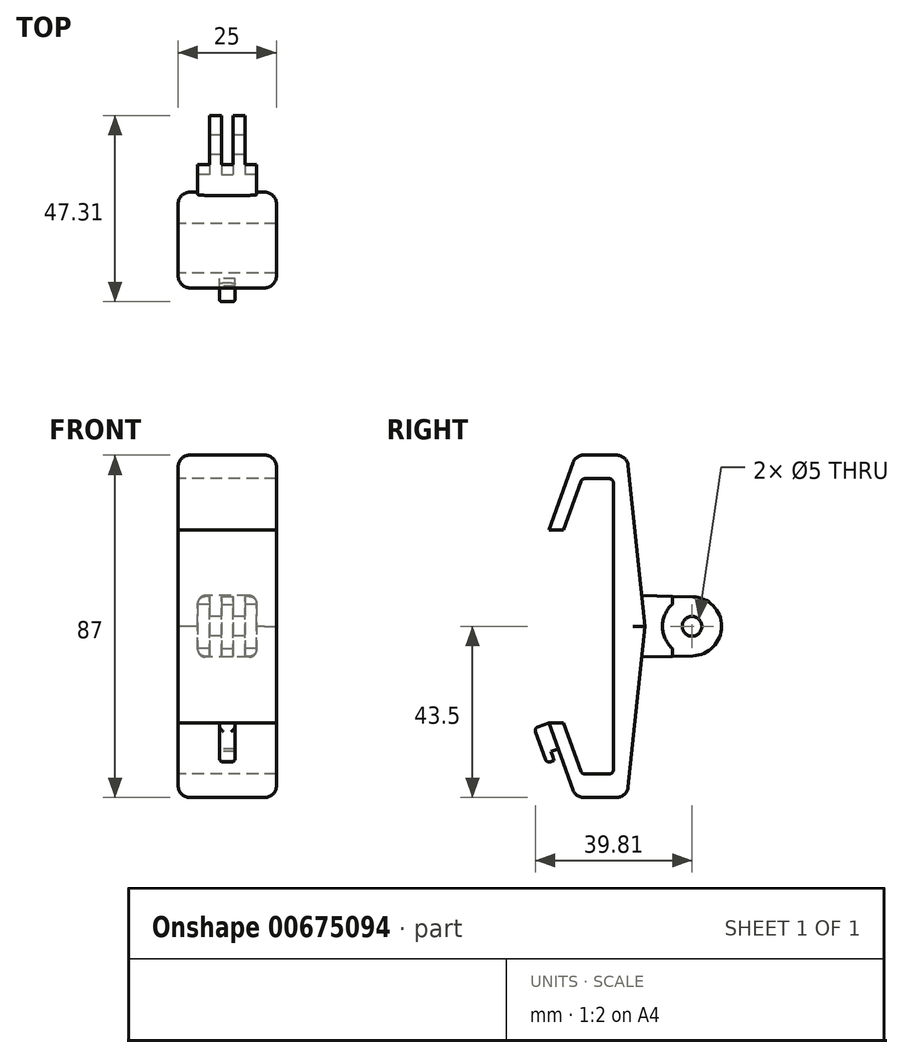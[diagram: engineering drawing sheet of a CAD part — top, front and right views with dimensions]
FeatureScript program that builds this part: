
annotation { "Feature Type Name" : "Feature", "Feature Type Description" : "" }
export const myFeature = defineFeature(function(context is Context, id is Id, definition is map)
    precondition{}
    {
        {
            var Q0;
            Q0=qCreatedBy(makeId("Right.planeOp"),FACE);
            var sketch = newSketch(context, id + "F0", { "sketchPlane" : qUnion([Q0])});
            skLineSegment(sketch, "E0", {"start": v(0, 37.5) * mm, "end": v(0, -37.5) * mm});
            skLineSegment(sketch, "E1", {"start": v(0, -37.5) * mm, "end": v(-8, -37.5) * mm});
            skLineSegment(sketch, "E2", {"start": v(-8, -37.5) * mm, "end": v(-12.6, -24.5) * mm});
            skLineSegment(sketch, "E3", {"start": v(-12.6, -24.5) * mm, "end": v(-16.31, -24.5) * mm});
            skLineSegment(sketch, "E4", {"start": v(-16.31, -24.5) * mm, "end": v(-9.59, -43.5) * mm});
            skLineSegment(sketch, "E5", {"start": v(-9.59, -43.5) * mm, "end": v(3.5, -43.5) * mm});
            skLineSegment(sketch, "E6", {"start": v(3.5, -43.5) * mm, "end": v(8, 0) * mm});
            skLineSegment(sketch, "E7", {"start": v(8, 0) * mm, "end": v(3.5, 43.5) * mm});
            skLineSegment(sketch, "E8", {"start": v(3.5, 43.5) * mm, "end": v(-9.59, 43.5) * mm});
            skLineSegment(sketch, "E9", {"start": v(-9.59, 43.5) * mm, "end": v(-16.31, 24.5) * mm});
            skLineSegment(sketch, "E10", {"start": v(-16.31, 24.5) * mm, "end": v(-12.6, 24.5) * mm});
            skLineSegment(sketch, "E11", {"start": v(-12.6, 24.5) * mm, "end": v(-8, 37.5) * mm});
            skLineSegment(sketch, "E12", {"start": v(-8, 37.5) * mm, "end": v(0, 37.5) * mm});
            skSolve(sketch);
        }
        {
            var Q0;
            Q0=makeQuery(id+"F0.imprint","IMPRINT",FACE,{"disambiguationData":[TD([[makeQuery(id+"F0.imprint","IMPRINT",EDGE,{"derivedFrom":sQuery(id+"F0.wireOp",EDGE,"E0")}),1.0]])]});
            extrude(context, id + "F1", {"entities" : qUnion([Q0]), "endBound" : BoundingType.SYMMETRIC, "depth" : 25 * mm, "offsetDistance" : 25 * mm});
        }
        {
            var Q0;
            Q0=qCreatedBy(makeId("Right.planeOp"),FACE);
            var sketch = newSketch(context, id + "F2", { "sketchPlane" : qUnion([Q0])});
            skCircle(sketch, "E13", {"center": v(20, 0) * mm, "radius": 2.5 * mm});
            skCircle(sketch, "E14", {"center": v(20, 0) * mm, "radius": 7.5 * mm});
            skLineSegment(sketch, "E15.0", {"start": v(8, 0) * mm, "end": v(3.5, 43.5) * mm});
            skLineSegment(sketch, "E16.0", {"start": v(3.5, -43.5) * mm, "end": v(8, 0) * mm});
            skLineSegment(sketch, "E17", {"start": v(7.19, 7.84) * mm, "end": v(20.2, 7.5) * mm});
            skLineSegment(sketch, "E18", {"start": v(7.19, -7.84) * mm, "end": v(20.2, -7.5) * mm});
            skLineSegment(sketch, "E19", {"start": v(15, 7.63) * mm, "end": v(15, -7.63) * mm});
            skSolve(sketch);
        }
        {
            var Q0;
            {var subQ7=sQuery(id+"F2.wireOp",EDGE,"E19");var subQ9=sQuery(id+"F2.wireOp",EDGE,"E14");var subQ10=makeQuery(id+"F2.imprint","INTERSECT",VERTEX,{"disambiguationData":[OD(0.0)],"derivedFrom":[subQ9,subQ7]});Q0=makeQuery(id+"F2.imprint","IMPRINT",FACE,{"disambiguationData":[TD([[makeQuery(id+"F2.imprint","IMPRINT",EDGE,{"disambiguationData":[TD([[subQ10,-1.0]])],"derivedFrom":subQ9}),-1.0]])]});}
            extrude(context, id + "F3", {"entities" : qUnion([Q0]), "operationType" : NewBodyOperationType.ADD, "endBound" : BoundingType.SYMMETRIC, "depth" : 15 * mm, "offsetDistance" : 25 * mm});
        }
        {
            var Q0;
            {var subQ0=sQuery(id+"F2.wireOp",EDGE,"E17");var subQ1=sQuery(id+"F2.wireOp",EDGE,"E14");var subQ2=makeQuery(id+"F2.imprint","INTERSECT",VERTEX,{"derivedFrom":[subQ1,subQ0]});Q0=makeQuery(id+"F2.imprint","IMPRINT",FACE,{"disambiguationData":[TD([[makeQuery(id+"F2.imprint","IMPRINT",EDGE,{"disambiguationData":[TD([[subQ2,-1.0]])],"derivedFrom":subQ1}),-1.0]])]});}
            var Q1;
            Q1=makeQuery(id+"F2.imprint","IMPRINT",FACE,{"disambiguationData":[TD([[makeQuery(id+"F2.imprint","IMPRINT",EDGE,{"derivedFrom":sQuery(id+"F2.wireOp",EDGE,"E13")}),-1.0]])]});
            var Q2;
            {var subQ0=sQuery(id+"F2.wireOp",EDGE,"E19");var subQ1=sQuery(id+"F2.wireOp",EDGE,"E14");var subQ2=makeQuery(id+"F2.imprint","INTERSECT",VERTEX,{"disambiguationData":[OD(0.0)],"derivedFrom":[subQ1,subQ0]});Q2=makeQuery(id+"F2.imprint","IMPRINT",FACE,{"disambiguationData":[TD([[makeQuery(id+"F2.imprint","IMPRINT",EDGE,{"disambiguationData":[TD([[subQ2,-1.0]])],"derivedFrom":subQ1}),1.0]])]});}
            var Q3;
            {var subQ0=sQuery(id+"F2.wireOp",EDGE,"E18");var subQ1=sQuery(id+"F2.wireOp",EDGE,"E14");var subQ2=makeQuery(id+"F2.imprint","INTERSECT",VERTEX,{"derivedFrom":[subQ1,subQ0]});Q3=makeQuery(id+"F2.imprint","IMPRINT",FACE,{"disambiguationData":[TD([[makeQuery(id+"F2.imprint","IMPRINT",EDGE,{"disambiguationData":[TD([[subQ2,1.0]])],"derivedFrom":subQ1}),-1.0]])]});}
            extrude(context, id + "F4", {"entities" : qUnion([Q0, Q1, Q2, Q3]), "operationType" : NewBodyOperationType.ADD, "endBound" : BoundingType.SYMMETRIC, "depth" : 9 * mm, "offsetDistance" : 25 * mm});
        }
        {
            var Q0;
            {var subQ0=sQuery(id+"F2.wireOp",EDGE,"E17");var subQ1=sQuery(id+"F2.wireOp",EDGE,"E14");var subQ2=makeQuery(id+"F2.imprint","INTERSECT",VERTEX,{"derivedFrom":[subQ1,subQ0]});Q0=makeQuery(id+"F2.imprint","IMPRINT",FACE,{"disambiguationData":[TD([[makeQuery(id+"F2.imprint","IMPRINT",EDGE,{"disambiguationData":[TD([[subQ2,-1.0]])],"derivedFrom":subQ1}),-1.0]])]});}
            var Q1;
            {var subQ0=sQuery(id+"F2.wireOp",EDGE,"E18");var subQ1=sQuery(id+"F2.wireOp",EDGE,"E14");var subQ2=makeQuery(id+"F2.imprint","INTERSECT",VERTEX,{"derivedFrom":[subQ1,subQ0]});Q1=makeQuery(id+"F2.imprint","IMPRINT",FACE,{"disambiguationData":[TD([[makeQuery(id+"F2.imprint","IMPRINT",EDGE,{"disambiguationData":[TD([[subQ2,1.0]])],"derivedFrom":subQ1}),-1.0]])]});}
            var Q2;
            Q2=makeQuery(id+"F2.imprint","IMPRINT",FACE,{"disambiguationData":[TD([[makeQuery(id+"F2.imprint","IMPRINT",EDGE,{"derivedFrom":sQuery(id+"F2.wireOp",EDGE,"E13")}),-1.0]])]});
            var Q3;
            {var subQ0=sQuery(id+"F2.wireOp",EDGE,"E19");var subQ1=sQuery(id+"F2.wireOp",EDGE,"E14");var subQ2=makeQuery(id+"F2.imprint","INTERSECT",VERTEX,{"disambiguationData":[OD(0.0)],"derivedFrom":[subQ1,subQ0]});Q3=makeQuery(id+"F2.imprint","IMPRINT",FACE,{"disambiguationData":[TD([[makeQuery(id+"F2.imprint","IMPRINT",EDGE,{"disambiguationData":[TD([[subQ2,-1.0]])],"derivedFrom":subQ1}),1.0]])]});}
            extrude(context, id + "F5", {"entities" : qUnion([Q0, Q1, Q2, Q3]), "operationType" : NewBodyOperationType.REMOVE, "endBound" : BoundingType.SYMMETRIC, "oppositeDirection" : true, "depth" : 3 * mm, "offsetDistance" : 25 * mm});
        }
        {
            var Q0;
            Q0=makeQuery(id+"F1.opExtrude","CAP_EDGE",EDGE,{"disambiguationData":[OSD([sQuery(id+"F0.wireOp",EDGE,"E7")])],"isStart":false});
            var Q1;
            Q1=makeQuery(id+"F1.opExtrude","CAP_EDGE",EDGE,{"disambiguationData":[OSD([sQuery(id+"F0.wireOp",EDGE,"E6")])],"isStart":false});
            var Q2;
            Q2=makeQuery(id+"F1.opExtrude","CAP_EDGE",EDGE,{"disambiguationData":[OSD([sQuery(id+"F0.wireOp",EDGE,"E5")])],"isStart":false});
            var Q3;
            Q3=makeQuery(id+"F1.opExtrude","CAP_EDGE",EDGE,{"disambiguationData":[OSD([sQuery(id+"F0.wireOp",EDGE,"E4")])],"isStart":false});
            var Q4;
            Q4=makeQuery(id+"F1.opExtrude","SWEPT_EDGE",EDGE,{"disambiguationData":[OSD([sQuery(id+"F0.wireOp",EDGE,"E4"),sQuery(id+"F0.wireOp",EDGE,"E5")])]});
            var Q5;
            Q5=makeQuery(id+"F1.opExtrude","CAP_EDGE",EDGE,{"disambiguationData":[OSD([sQuery(id+"F0.wireOp",EDGE,"E4")])],"isStart":true});
            var Q6;
            Q6=makeQuery(id+"F1.opExtrude","CAP_EDGE",EDGE,{"disambiguationData":[OSD([sQuery(id+"F0.wireOp",EDGE,"E6")])],"isStart":true});
            var Q7;
            Q7=makeQuery(id+"F1.opExtrude","CAP_EDGE",EDGE,{"disambiguationData":[OSD([sQuery(id+"F0.wireOp",EDGE,"E5")])],"isStart":true});
            var Q8;
            Q8=makeQuery(id+"F1.opExtrude","CAP_EDGE",EDGE,{"disambiguationData":[OSD([sQuery(id+"F0.wireOp",EDGE,"E7")])],"isStart":true});
            var Q9;
            Q9=makeQuery(id+"F1.opExtrude","SWEPT_EDGE",EDGE,{"disambiguationData":[OSD([sQuery(id+"F0.wireOp",EDGE,"E7"),sQuery(id+"F0.wireOp",EDGE,"E8")])]});
            var Q10;
            Q10=makeQuery(id+"F1.opExtrude","SWEPT_EDGE",EDGE,{"disambiguationData":[OSD([sQuery(id+"F0.wireOp",EDGE,"E5"),sQuery(id+"F0.wireOp",EDGE,"E6")])]});
            var Q11;
            Q11=makeQuery(id+"F1.opExtrude","SWEPT_EDGE",EDGE,{"disambiguationData":[OSD([sQuery(id+"F0.wireOp",EDGE,"E8"),sQuery(id+"F0.wireOp",EDGE,"E9")])]});
            var Q12;
            Q12=makeQuery(id+"F1.opExtrude","CAP_EDGE",EDGE,{"disambiguationData":[OSD([sQuery(id+"F0.wireOp",EDGE,"E8")])],"isStart":true});
            var Q13;
            Q13=makeQuery(id+"F1.opExtrude","CAP_EDGE",EDGE,{"disambiguationData":[OSD([sQuery(id+"F0.wireOp",EDGE,"E9")])],"isStart":true});
            var Q14;
            Q14=makeQuery(id+"F1.opExtrude","CAP_EDGE",EDGE,{"disambiguationData":[OSD([sQuery(id+"F0.wireOp",EDGE,"E9")])],"isStart":false});
            var Q15;
            Q15=makeQuery(id+"F1.opExtrude","CAP_EDGE",EDGE,{"disambiguationData":[OSD([sQuery(id+"F0.wireOp",EDGE,"E8")])],"isStart":false});
            fillet(context, id + "F6", {"entities" : qUnion([Q0, Q1, Q2, Q3, Q4, Q5, Q6, Q7, Q8, Q9, Q10, Q11, Q12, Q13, Q14, Q15]), "radius" : 3 * mm, "tangentPropagation" : true, "allowEdgeOverflow" : false});
        }
        {
            var Q0;
            Q0=makeQuery(id+"F3.opExtrude","SWEPT_EDGE",EDGE,{"disambiguationData":[OSD([sQuery(id+"F2.wireOp",EDGE,"E15.0"),sQuery(id+"F2.wireOp",EDGE,"E17")])]});
            var Q1;
            Q1=makeQuery(id+"F3.opExtrude","CAP_EDGE",EDGE,{"disambiguationData":[OSD([sQuery(id+"F2.wireOp",EDGE,"E15.0")])],"isStart":true});
            var Q2;
            Q2=makeQuery(id+"F3.opExtrude","CAP_EDGE",EDGE,{"disambiguationData":[OSD([sQuery(id+"F2.wireOp",EDGE,"E16.0")])],"isStart":true});
            var Q3;
            Q3=makeQuery(id+"F3.opExtrude","SWEPT_EDGE",EDGE,{"disambiguationData":[OSD([sQuery(id+"F2.wireOp",EDGE,"E16.0"),sQuery(id+"F2.wireOp",EDGE,"E18")])]});
            var Q4;
            Q4=makeQuery(id+"F3.opExtrude","CAP_EDGE",EDGE,{"disambiguationData":[OSD([sQuery(id+"F2.wireOp",EDGE,"E16.0")])],"isStart":false});
            var Q5;
            Q5=makeQuery(id+"F3.opExtrude","CAP_EDGE",EDGE,{"disambiguationData":[OSD([sQuery(id+"F2.wireOp",EDGE,"E15.0")])],"isStart":false});
            var Q6;
            Q6=makeQuery(id+"F3.opExtrude","CAP_EDGE",EDGE,{"disambiguationData":[OSD([sQuery(id+"F2.wireOp",EDGE,"E17")])],"isStart":false});
            var Q7;
            Q7=makeQuery(id+"F3.opExtrude","CAP_EDGE",EDGE,{"disambiguationData":[OSD([sQuery(id+"F2.wireOp",EDGE,"E18")])],"isStart":false});
            var Q8;
            Q8=makeQuery(id+"F3.opExtrude","CAP_EDGE",EDGE,{"disambiguationData":[OSD([sQuery(id+"F2.wireOp",EDGE,"E18")])],"isStart":true});
            var Q9;
            Q9=makeQuery(id+"F3.opExtrude","CAP_EDGE",EDGE,{"disambiguationData":[OSD([sQuery(id+"F2.wireOp",EDGE,"E17")])],"isStart":true});
            fillet(context, id + "F7", {"entities" : qUnion([Q0, Q1, Q2, Q3, Q4, Q5, Q6, Q7, Q8, Q9]), "radius" : 2 * mm, "tangentPropagation" : true, "allowEdgeOverflow" : false});
        }
        {
            var Q0;
            Q0=makeQuery(id+"F1.opExtrude","SWEPT_FACE",FACE,{"disambiguationData":[OSD([sQuery(id+"F0.wireOp",EDGE,"E4")])]});
            var sketch = newSketch(context, id + "F8", { "sketchPlane" : qUnion([Q0])});
            skLineSegment(sketch, "E20.bottom", {"start": v(-2, -17.66) * mm, "end": v(2, -17.66) * mm});
            skLineSegment(sketch, "E20.top", {"start": v(-2, -27.16) * mm, "end": v(2, -27.16) * mm});
            skLineSegment(sketch, "E20.left", {"start": v(-2, -17.66) * mm, "end": v(-2, -27.16) * mm});
            skLineSegment(sketch, "E20.right", {"start": v(2, -17.66) * mm, "end": v(2, -27.16) * mm});
            skPoint(sketch, "E20.middle", {"position": v(0, -22.4) * mm});
            skPoint(sketch, "E20.middle.positionSnap0", {"position": v(0, -17.66) * mm});
            skPoint(sketch, "E20.centerSnap0", {"position": v(0, -17.66) * mm});
            skLineSegment(sketch, "E21", {"start": v(2, -24.66) * mm, "end": v(-2, -24.66) * mm});
            skSolve(sketch);
        }
        {
            var Q0;
            {var subQ0=sQuery(id+"F8.wireOp",EDGE,"E20.bottom");Q0=makeQuery(id+"F8.imprint","IMPRINT",FACE,{"disambiguationData":[TD([[makeQuery(id+"F8.imprint","IMPRINT",EDGE,{"derivedFrom":subQ0}),1.0]])]});}
            var Q1;
            {var subQ0=sQuery(id+"F8.wireOp",EDGE,"E20.top");Q1=makeQuery(id+"F8.imprint","IMPRINT",FACE,{"disambiguationData":[TD([[makeQuery(id+"F8.imprint","IMPRINT",EDGE,{"derivedFrom":subQ0}),1.0]])]});}
            extrude(context, id + "F9", {"entities" : qUnion([Q0, Q1]), "operationType" : NewBodyOperationType.ADD, "depth" : 4 * mm, "offsetDistance" : 25 * mm});
        }
        {
            var Q0;
            {var subQ0=sQuery(id+"F8.wireOp",EDGE,"E20.top");Q0=makeQuery(id+"F8.imprint","IMPRINT",FACE,{"disambiguationData":[TD([[makeQuery(id+"F8.imprint","IMPRINT",EDGE,{"derivedFrom":subQ0}),1.0]])]});}
            extrude(context, id + "F10", {"entities" : qUnion([Q0]), "operationType" : NewBodyOperationType.REMOVE, "depth" : 2 * mm, "offsetDistance" : 25 * mm});
        }
        {
            var Q0;
            Q0=makeQuery(id+"FVgPiMfgENfQ3i9_1.1.F9.opExtrude","CAP_EDGE",EDGE,{"disambiguationData":[OSD([sQuery(id+"F8.wireOp",EDGE,"E20.left")])],"isStart":true});
            var Q1;
            Q1=makeQuery(id+"FVgPiMfgENfQ3i9_1.1.F9.opExtrude","CAP_EDGE",EDGE,{"disambiguationData":[OSD([sQuery(id+"F8.wireOp",EDGE,"E20.right")])],"isStart":true});
            var Q2;
            Q2=makeQuery(id+"FVgPiMfgENfQ3i9_1.1.F9.opExtrude","CAP_FACE",FACE,{"disambiguationData":[OSD([sQuery(id+"F8.wireOp",EDGE,"E20.bottom"),sQuery(id+"F8.wireOp",EDGE,"E20.top"),sQuery(id+"F8.wireOp",EDGE,"E20.left"),sQuery(id+"F8.wireOp",EDGE,"E20.right")])],"isStart":false});
            var Q3;
            Q3=makeQuery(id+"FVgPiMfgENfQ3i9_1.1.F9.opExtrude","SWEPT_EDGE",EDGE,{"disambiguationData":[OSD([sQuery(id+"F8.wireOp",EDGE,"E20.top"),sQuery(id+"F8.wireOp",EDGE,"E20.right")])]});
            var Q4;
            Q4=makeQuery(id+"FVgPiMfgENfQ3i9_1.1.F9.opExtrude","SWEPT_EDGE",EDGE,{"disambiguationData":[OSD([sQuery(id+"F8.wireOp",EDGE,"E20.top"),sQuery(id+"F8.wireOp",EDGE,"E20.left")])]});
            var Q5;
            Q5=makeQuery(id+"F9.opExtrude","CAP_FACE",FACE,{"disambiguationData":[OSD([sQuery(id+"F8.wireOp",EDGE,"E20.bottom"),sQuery(id+"F8.wireOp",EDGE,"E20.top"),sQuery(id+"F8.wireOp",EDGE,"E20.left"),sQuery(id+"F8.wireOp",EDGE,"E20.right")])],"isStart":false});
            var Q6;
            Q6=makeQuery(id+"F9.opExtrude","CAP_EDGE",EDGE,{"disambiguationData":[OSD([sQuery(id+"F8.wireOp",EDGE,"E20.left")])],"isStart":true});
            var Q7;
            Q7=makeQuery(id+"F9.opExtrude","CAP_EDGE",EDGE,{"disambiguationData":[OSD([sQuery(id+"F8.wireOp",EDGE,"E20.right")])],"isStart":true});
            var Q8;
            Q8=makeQuery(id+"F9.opExtrude","SWEPT_EDGE",EDGE,{"disambiguationData":[OSD([sQuery(id+"F8.wireOp",EDGE,"E20.top"),sQuery(id+"F8.wireOp",EDGE,"E20.right")])]});
            var Q9;
            Q9=makeQuery(id+"F9.opExtrude","SWEPT_EDGE",EDGE,{"disambiguationData":[OSD([sQuery(id+"F8.wireOp",EDGE,"E20.top"),sQuery(id+"F8.wireOp",EDGE,"E20.left")])]});
            fillet(context, id + "F11", {"entities" : qUnion([Q0, Q1, Q2, Q3, Q4, Q5, Q6, Q7, Q8, Q9]), "radius" : 1 * mm, "tangentPropagation" : true, "allowEdgeOverflow" : false});
        }
        {
            var Q0;
            Q0=makeQuery(id+"F1.opExtrude","SWEPT_EDGE",EDGE,{"disambiguationData":[OSD([sQuery(id+"F0.wireOp",EDGE,"E0"),sQuery(id+"F0.wireOp",EDGE,"E1")])]});
            var Q1;
            Q1=makeQuery(id+"F1.opExtrude","SWEPT_EDGE",EDGE,{"disambiguationData":[OSD([sQuery(id+"F0.wireOp",EDGE,"E1"),sQuery(id+"F0.wireOp",EDGE,"E2")])]});
            var Q2;
            Q2=makeQuery(id+"F1.opExtrude","SWEPT_EDGE",EDGE,{"disambiguationData":[OSD([sQuery(id+"F0.wireOp",EDGE,"E0"),sQuery(id+"F0.wireOp",EDGE,"E12")])]});
            var Q3;
            Q3=makeQuery(id+"F1.opExtrude","SWEPT_EDGE",EDGE,{"disambiguationData":[OSD([sQuery(id+"F0.wireOp",EDGE,"E11"),sQuery(id+"F0.wireOp",EDGE,"E12")])]});
            fillet(context, id + "F12", {"entities" : qUnion([Q0, Q1, Q2, Q3]), "radius" : 1 * mm, "tangentPropagation" : true, "allowEdgeOverflow" : false});
        }
    });
